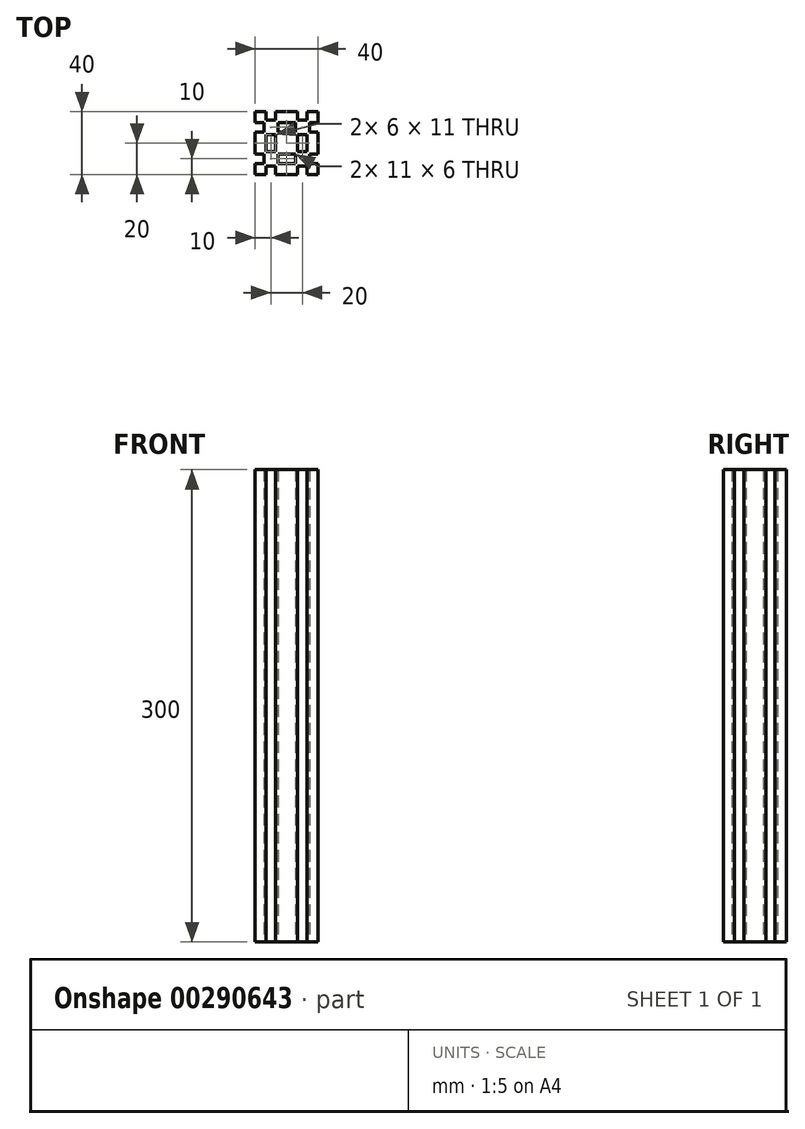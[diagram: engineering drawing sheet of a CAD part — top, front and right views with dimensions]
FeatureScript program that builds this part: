
annotation { "Feature Type Name" : "Feature", "Feature Type Description" : "" }
export const myFeature = defineFeature(function(context is Context, id is Id, definition is map)
    precondition{}
    {
        {
            var Q0;
            Q0=qCreatedBy(makeId("Top.planeOp"),FACE);
            var sketch = newSketch(context, id + "F0", { "sketchPlane" : qUnion([Q0])});
            skLineSegment(sketch, "E0.bottom", {"start": v(0, 0) * mm, "end": v(20, 0) * mm});
            skLineSegment(sketch, "E0.top", {"start": v(0, 20) * mm, "end": v(20, 20) * mm});
            skLineSegment(sketch, "E0.left", {"start": v(0, 0) * mm, "end": v(0, 20) * mm});
            skLineSegment(sketch, "E0.right", {"start": v(20, 0) * mm, "end": v(20, 20) * mm});
            skLineSegment(sketch, "E1.bottom", {"start": v(7, 20) * mm, "end": v(13, 20) * mm});
            skLineSegment(sketch, "E1.top", {"start": v(7, 14.5) * mm, "end": v(13, 14.5) * mm});
            skLineSegment(sketch, "E1.left", {"start": v(7, 20) * mm, "end": v(7, 14.5) * mm});
            skLineSegment(sketch, "E1.right", {"start": v(13, 20) * mm, "end": v(13, 14.5) * mm});
            skLineSegment(sketch, "E2.bottom", {"start": v(20, 13) * mm, "end": v(14.5, 13) * mm});
            skLineSegment(sketch, "E2.top", {"start": v(20, 7) * mm, "end": v(14.5, 7) * mm});
            skLineSegment(sketch, "E2.left", {"start": v(20, 13) * mm, "end": v(20, 7) * mm});
            skLineSegment(sketch, "E2.right", {"start": v(14.5, 13) * mm, "end": v(14.5, 7) * mm});
            skLineSegment(sketch, "E3.bottom", {"start": v(13, 0) * mm, "end": v(7, 0) * mm});
            skLineSegment(sketch, "E3.top", {"start": v(13, 5.5) * mm, "end": v(7, 5.5) * mm});
            skLineSegment(sketch, "E3.left", {"start": v(13, 0) * mm, "end": v(13, 5.5) * mm});
            skLineSegment(sketch, "E3.right", {"start": v(7, 0) * mm, "end": v(7, 5.5) * mm});
            skLineSegment(sketch, "E4.bottom", {"start": v(0, 7) * mm, "end": v(5.5, 7) * mm});
            skLineSegment(sketch, "E4.top", {"start": v(0, 13) * mm, "end": v(5.5, 13) * mm});
            skLineSegment(sketch, "E4.left", {"start": v(0, 7) * mm, "end": v(0, 13) * mm});
            skLineSegment(sketch, "E4.right", {"start": v(5.5, 7) * mm, "end": v(5.5, 13) * mm});
            skLineSegment(sketch, "E5.MirrorCS", {"start": v(0, 13) * mm, "end": v(-5.5, 13) * mm});
            skLineSegment(sketch, "E6.MirrorCS", {"start": v(0, 7) * mm, "end": v(-5.5, 7) * mm});
            skLineSegment(sketch, "E7.MirrorCS", {"start": v(-13, 0) * mm, "end": v(-7, 0) * mm});
            skLineSegment(sketch, "E8.MirrorCS", {"start": v(-14.5, 13) * mm, "end": v(-14.5, 7) * mm});
            skLineSegment(sketch, "E9.MirrorCS", {"start": v(-20, 13) * mm, "end": v(-20, 7) * mm});
            skLineSegment(sketch, "E10.MirrorCS", {"start": v(-20, 7) * mm, "end": v(-14.5, 7) * mm});
            skLineSegment(sketch, "E11.MirrorCS", {"start": v(-20, 13) * mm, "end": v(-14.5, 13) * mm});
            skLineSegment(sketch, "E12.MirrorCS", {"start": v(-13, 20) * mm, "end": v(-13, 14.5) * mm});
            skLineSegment(sketch, "E13.MirrorCS", {"start": v(-7, 20) * mm, "end": v(-7, 14.5) * mm});
            skLineSegment(sketch, "E14.MirrorCS", {"start": v(-7, 14.5) * mm, "end": v(-13, 14.5) * mm});
            skLineSegment(sketch, "E15.MirrorCS", {"start": v(-7, 20) * mm, "end": v(-13, 20) * mm});
            skLineSegment(sketch, "E16.MirrorCS", {"start": v(-20, 0) * mm, "end": v(-20, 20) * mm});
            skLineSegment(sketch, "E17.MirrorCS", {"start": v(0, 20) * mm, "end": v(-20, 20) * mm});
            skLineSegment(sketch, "E18.MirrorCS", {"start": v(0, 0) * mm, "end": v(-20, 0) * mm});
            skLineSegment(sketch, "E19.MirrorCS", {"start": v(-7, 0) * mm, "end": v(-7, 5.5) * mm});
            skLineSegment(sketch, "E20.MirrorCS", {"start": v(-13, 0) * mm, "end": v(-13, 5.5) * mm});
            skLineSegment(sketch, "E21.MirrorCS", {"start": v(-13, 5.5) * mm, "end": v(-7, 5.5) * mm});
            skLineSegment(sketch, "E22.MirrorCS", {"start": v(-5.5, 7) * mm, "end": v(-5.5, 13) * mm});
            skLineSegment(sketch, "E23.MirrorCS", {"start": v(0, -7) * mm, "end": v(0, -13) * mm});
            skLineSegment(sketch, "E24.MirrorCS", {"start": v(-20, -7) * mm, "end": v(-14.5, -7) * mm});
            skLineSegment(sketch, "E25.MirrorCS", {"start": v(5.5, -7) * mm, "end": v(5.5, -13) * mm});
            skLineSegment(sketch, "E26.MirrorCS", {"start": v(-7, 0) * mm, "end": v(-7, -5.5) * mm});
            skLineSegment(sketch, "E27.MirrorCS", {"start": v(13, -5.5) * mm, "end": v(7, -5.5) * mm});
            skLineSegment(sketch, "E28.MirrorCS", {"start": v(13, 0) * mm, "end": v(13, -5.5) * mm});
            skLineSegment(sketch, "E29.MirrorCS", {"start": v(7, 0) * mm, "end": v(7, -5.5) * mm});
            skLineSegment(sketch, "E30.MirrorCS", {"start": v(0, -20) * mm, "end": v(20, -20) * mm});
            skLineSegment(sketch, "E31.MirrorCS", {"start": v(0, 0) * mm, "end": v(0, -20) * mm});
            skLineSegment(sketch, "E32.MirrorCS", {"start": v(20, 0) * mm, "end": v(20, -20) * mm});
            skLineSegment(sketch, "E33.MirrorCS", {"start": v(7, -20) * mm, "end": v(13, -20) * mm});
            skLineSegment(sketch, "E34.MirrorCS", {"start": v(7, -14.5) * mm, "end": v(13, -14.5) * mm});
            skLineSegment(sketch, "E35.MirrorCS", {"start": v(7, -20) * mm, "end": v(7, -14.5) * mm});
            skLineSegment(sketch, "E36.MirrorCS", {"start": v(13, -20) * mm, "end": v(13, -14.5) * mm});
            skLineSegment(sketch, "E37.MirrorCS", {"start": v(20, -13) * mm, "end": v(14.5, -13) * mm});
            skLineSegment(sketch, "E38.MirrorCS", {"start": v(20, -7) * mm, "end": v(14.5, -7) * mm});
            skLineSegment(sketch, "E39.MirrorCS", {"start": v(20, -13) * mm, "end": v(20, -7) * mm});
            skLineSegment(sketch, "E40.MirrorCS", {"start": v(14.5, -13) * mm, "end": v(14.5, -7) * mm});
            skLineSegment(sketch, "E41.MirrorCS", {"start": v(-20, -13) * mm, "end": v(-14.5, -13) * mm});
            skLineSegment(sketch, "E42.MirrorCS", {"start": v(-7, -20) * mm, "end": v(-13, -20) * mm});
            skLineSegment(sketch, "E43.MirrorCS", {"start": v(0, -20) * mm, "end": v(-20, -20) * mm});
            skLineSegment(sketch, "E44.MirrorCS", {"start": v(0, -13) * mm, "end": v(5.5, -13) * mm});
            skLineSegment(sketch, "E45.MirrorCS", {"start": v(-14.5, -13) * mm, "end": v(-14.5, -7) * mm});
            skLineSegment(sketch, "E46.MirrorCS", {"start": v(-13, 0) * mm, "end": v(-13, -5.5) * mm});
            skLineSegment(sketch, "E47.MirrorCS", {"start": v(0, -13) * mm, "end": v(-5.5, -13) * mm});
            skLineSegment(sketch, "E48.MirrorCS", {"start": v(-13, -20) * mm, "end": v(-13, -14.5) * mm});
            skLineSegment(sketch, "E49.MirrorCS", {"start": v(-7, -20) * mm, "end": v(-7, -14.5) * mm});
            skLineSegment(sketch, "E50.MirrorCS", {"start": v(0, -7) * mm, "end": v(5.5, -7) * mm});
            skLineSegment(sketch, "E51.MirrorCS", {"start": v(-20, 0) * mm, "end": v(-20, -20) * mm});
            skLineSegment(sketch, "E52.MirrorCS", {"start": v(-7, -14.5) * mm, "end": v(-13, -14.5) * mm});
            skLineSegment(sketch, "E53.MirrorCS", {"start": v(-13, -5.5) * mm, "end": v(-7, -5.5) * mm});
            skLineSegment(sketch, "E54.MirrorCS", {"start": v(-20, -13) * mm, "end": v(-20, -7) * mm});
            skLineSegment(sketch, "E55.MirrorCS", {"start": v(-5.5, -7) * mm, "end": v(-5.5, -13) * mm});
            skLineSegment(sketch, "E56.MirrorCS", {"start": v(0, -7) * mm, "end": v(-5.5, -7) * mm});
            skSolve(sketch);
        }
        {
            var Q0;
            Q0=makeQuery(id+"F0.imprint","IMPRINT",FACE,{"disambiguationData":[TD([[makeQuery(id+"F0.imprint","IMPRINT",EDGE,{"derivedFrom":sQuery(id+"F0.wireOp",EDGE,"E1.top")}),-1.0]])]});
            var Q1;
            {var subQ5=sQuery(id+"F0.wireOp",EDGE,"E5.MirrorCS");Q1=makeQuery(id+"F0.imprint","IMPRINT",FACE,{"disambiguationData":[TD([[makeQuery(id+"F0.imprint","IMPRINT",EDGE,{"derivedFrom":subQ5}),-1.0]])]});}
            var Q2;
            {var subQ6=sQuery(id+"F0.wireOp",EDGE,"E24.MirrorCS");Q2=makeQuery(id+"F0.imprint","IMPRINT",FACE,{"disambiguationData":[TD([[makeQuery(id+"F0.imprint","IMPRINT",EDGE,{"derivedFrom":subQ6}),1.0]])]});}
            var Q3;
            Q3=makeQuery(id+"F0.imprint","IMPRINT",FACE,{"disambiguationData":[TD([[makeQuery(id+"F0.imprint","IMPRINT",EDGE,{"derivedFrom":sQuery(id+"F0.wireOp",EDGE,"E25.MirrorCS")}),1.0]])]});
            extrude(context, id + "F1", {"entities" : qUnion([Q0, Q1, Q2, Q3]), "depth" : 300 * mm});
        }
    });
